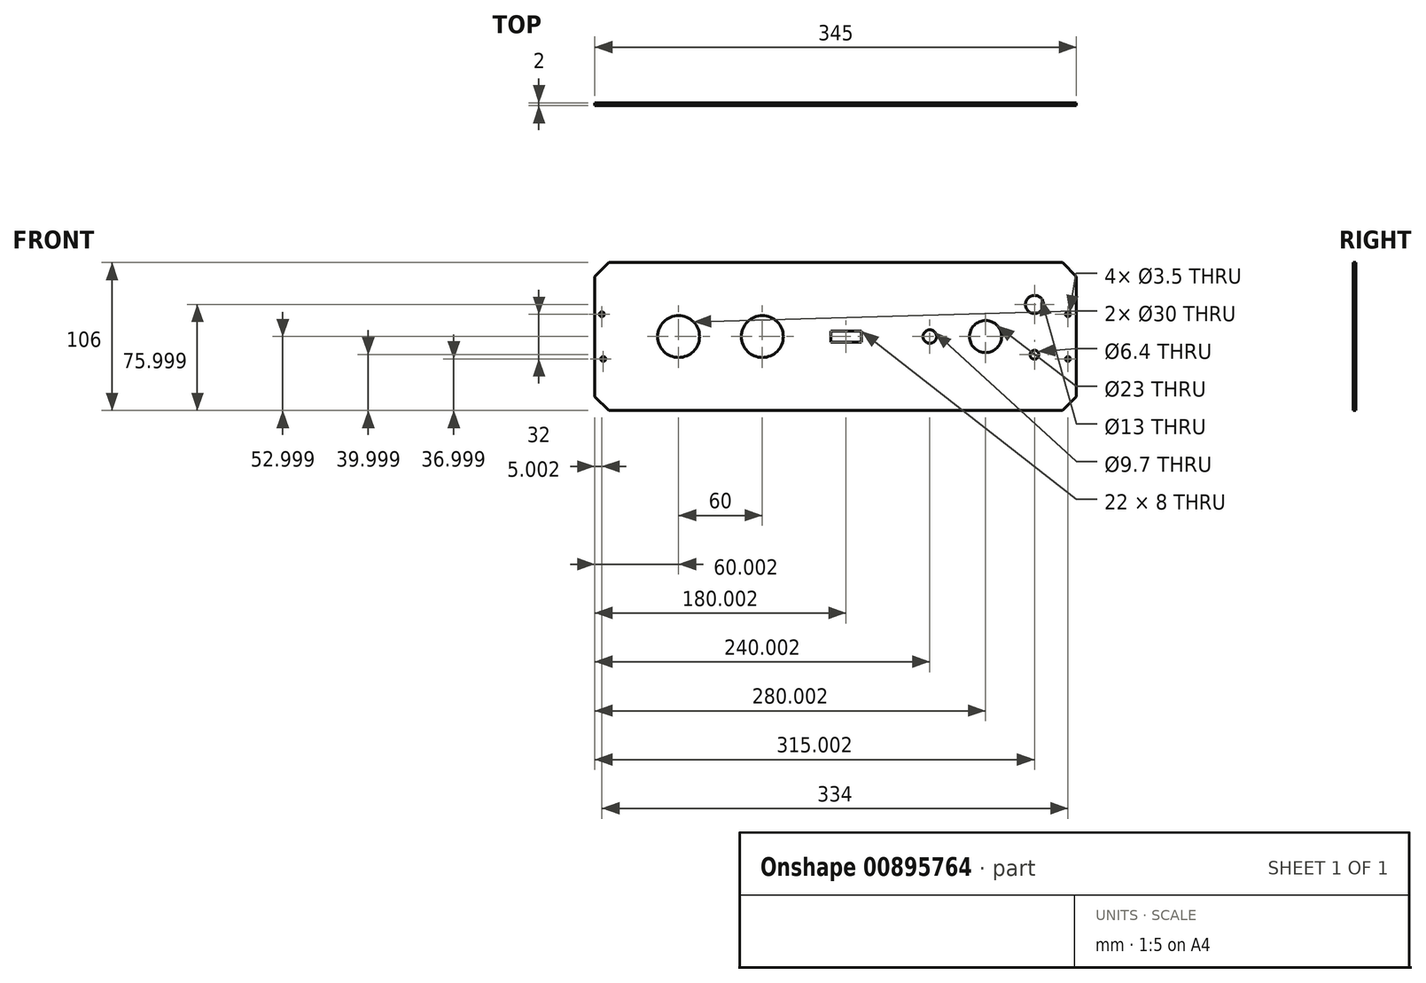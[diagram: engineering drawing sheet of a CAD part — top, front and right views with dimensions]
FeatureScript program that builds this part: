
annotation { "Feature Type Name" : "Feature", "Feature Type Description" : "" }
export const myFeature = defineFeature(function(context is Context, id is Id, definition is map)
    precondition{}
    {
        {
            var Q0;
            Q0=qCreatedBy(makeId("Front.planeOp"),FACE);
            var sketch = newSketch(context, id + "F0", { "sketchPlane" : qUnion([Q0])});
            skLineSegment(sketch, "E0.bottom", {"start": v(-126.34, 82.68) * mm, "end": v(218.66, 82.68) * mm});
            skLineSegment(sketch, "E0.top", {"start": v(-126.34, -23.32) * mm, "end": v(218.66, -23.32) * mm});
            skLineSegment(sketch, "E0.left", {"start": v(-126.34, 82.68) * mm, "end": v(-126.34, -23.32) * mm});
            skLineSegment(sketch, "E0.right", {"start": v(218.66, 82.68) * mm, "end": v(218.66, -23.32) * mm});
            skSolve(sketch);
        }
        {
            var Q0;
            Q0=makeQuery(id+"F0.imprint","IMPRINT",FACE,{"disambiguationData":[TD([[makeQuery(id+"F0.imprint","IMPRINT",EDGE,{"derivedFrom":sQuery(id+"F0.wireOp",EDGE,"E0.bottom")}),-1.0]])]});
            extrude(context, id + "F1", {"entities" : qUnion([Q0]), "depth" : 2 * mm, "offsetDistance" : 25 * mm});
        }
        {
            var Q0;
            Q0=makeQuery(id+"F1.opExtrude","SWEPT_EDGE",EDGE,{"disambiguationData":[OSD([sQuery(id+"F0.wireOp",EDGE,"E0.bottom"),sQuery(id+"F0.wireOp",EDGE,"E0.left")])]});
            chamfer(context, id + "F2", {"entities" : qUnion([Q0]), "width" : 10 * mm, "tangentPropagation" : true});
        }
        {
            var Q0;
            Q0=makeQuery(id+"F1.opExtrude","SWEPT_EDGE",EDGE,{"disambiguationData":[OSD([sQuery(id+"F0.wireOp",EDGE,"E0.top"),sQuery(id+"F0.wireOp",EDGE,"E0.left")])]});
            var Q1;
            Q1=makeQuery(id+"F1.opExtrude","SWEPT_EDGE",EDGE,{"disambiguationData":[OSD([sQuery(id+"F0.wireOp",EDGE,"E0.top"),sQuery(id+"F0.wireOp",EDGE,"E0.right")])]});
            var Q2;
            Q2=makeQuery(id+"F1.opExtrude","SWEPT_EDGE",EDGE,{"disambiguationData":[OSD([sQuery(id+"F0.wireOp",EDGE,"E0.bottom"),sQuery(id+"F0.wireOp",EDGE,"E0.right")])]});
            chamfer(context, id + "F3", {"entities" : qUnion([Q0, Q1, Q2]), "width" : 10 * mm, "tangentPropagation" : true});
        }
        {
            var Q0;
            Q0=makeQuery(id+"F1.opExtrude","CAP_FACE",FACE,{"disambiguationData":[OSD([sQuery(id+"F0.wireOp",EDGE,"E0.bottom"),sQuery(id+"F0.wireOp",EDGE,"E0.top"),sQuery(id+"F0.wireOp",EDGE,"E0.left"),sQuery(id+"F0.wireOp",EDGE,"E0.right")])],"isStart":false});
            var sketch = newSketch(context, id + "F4", { "sketchPlane" : qUnion([Q0])});
            skCircle(sketch, "E1", {"center": v(-121.34, 45.68) * mm, "radius": 1.75 * mm});
            skCircle(sketch, "E2", {"center": v(-120.34, 13.68) * mm, "radius": 1.75 * mm});
            skCircle(sketch, "E3", {"center": v(212.66, 45.68) * mm, "radius": 1.75 * mm});
            skCircle(sketch, "E4", {"center": v(212.66, 13.68) * mm, "radius": 1.75 * mm});
            skSolve(sketch);
        }
        {
            var Q0;
            Q0 = qSketchRegion(id + "F4", true);
            extrude(context, id + "F5", {"entities" : qUnion([Q0]), "operationType" : NewBodyOperationType.REMOVE, "oppositeDirection" : true, "depth" : 25 * mm, "offsetDistance" : 25 * mm});
        }
        {
            var Q0;
            Q0=makeQuery(id+"F1.opExtrude","CAP_FACE",FACE,{"disambiguationData":[OSD([sQuery(id+"F0.wireOp",EDGE,"E0.bottom"),sQuery(id+"F0.wireOp",EDGE,"E0.top"),sQuery(id+"F0.wireOp",EDGE,"E0.left"),sQuery(id+"F0.wireOp",EDGE,"E0.right")])],"isStart":false});
            var sketch = newSketch(context, id + "F6", { "sketchPlane" : qUnion([Q0])});
            skCircle(sketch, "E5", {"center": v(-66.34, 29.68) * mm, "radius": 15 * mm});
            skCircle(sketch, "E6", {"center": v(-6.34, 29.68) * mm, "radius": 15 * mm});
            skLineSegment(sketch, "E7.bottom", {"start": v(64.66, 33.68) * mm, "end": v(42.66, 33.68) * mm});
            skLineSegment(sketch, "E7.top", {"start": v(64.66, 25.68) * mm, "end": v(42.66, 25.68) * mm});
            skLineSegment(sketch, "E7.left", {"start": v(64.66, 33.68) * mm, "end": v(64.66, 25.68) * mm});
            skLineSegment(sketch, "E7.right", {"start": v(42.66, 33.68) * mm, "end": v(42.66, 25.68) * mm});
            skPoint(sketch, "E7.middle", {"position": v(53.66, 29.68) * mm});
            skPoint(sketch, "E8.middle", {"position": v(113.66, 29.68) * mm});
            skPoint(sketch, "E8.bottom.end.orphan", {"position": v(109.56, 38.1) * mm});
            skPoint(sketch, "E8.bottom.start.orphan", {"position": v(117.76, 38.1) * mm});
            skPoint(sketch, "E8.top.end.orphan", {"position": v(109.56, 21.27) * mm});
            skPoint(sketch, "E8.top.start.orphan", {"position": v(117.76, 21.27) * mm});
            skCircle(sketch, "E9", {"center": v(113.66, 29.68) * mm, "radius": 4.85 * mm});
            skSolve(sketch);
        }
        {
            var Q0;
            Q0=makeQuery(id+"F6.imprint","IMPRINT",FACE,{"disambiguationData":[TD([[makeQuery(id+"F6.imprint","IMPRINT",EDGE,{"derivedFrom":sQuery(id+"F6.wireOp",EDGE,"E5")}),1.0]])]});
            var Q1;
            Q1=makeQuery(id+"F6.imprint","IMPRINT",FACE,{"disambiguationData":[TD([[makeQuery(id+"F6.imprint","IMPRINT",EDGE,{"derivedFrom":sQuery(id+"F6.wireOp",EDGE,"E6")}),1.0]])]});
            var Q2;
            Q2=makeQuery(id+"F6.imprint","IMPRINT",FACE,{"disambiguationData":[TD([[makeQuery(id+"F6.imprint","IMPRINT",EDGE,{"derivedFrom":sQuery(id+"F6.wireOp",EDGE,"E7.bottom")}),1.0]])]});
            var Q3;
            Q3=makeQuery(id+"F6.imprint","IMPRINT",FACE,{"disambiguationData":[TD([[makeQuery(id+"F6.imprint","IMPRINT",EDGE,{"derivedFrom":sQuery(id+"F6.wireOp",EDGE,"ImCfHW0b-P2D1-mjxa-g2fg-wQ2FQqMqRvlU")}),1.0]])]});
            var Q4;
            Q4=makeQuery(id+"F6.imprint","IMPRINT",FACE,{"disambiguationData":[TD([[makeQuery(id+"F6.imprint","IMPRINT",EDGE,{"derivedFrom":sQuery(id+"F6.wireOp",EDGE,"oKTFB2zu-I9cH-oKnA-bQDt-sKLei0EZkSTM.bottom")}),1.0]])]});
            extrude(context, id + "F7", {"entities" : qUnion([Q0, Q1, Q2, Q3, Q4]), "operationType" : NewBodyOperationType.REMOVE, "oppositeDirection" : true, "depth" : 25 * mm, "offsetDistance" : 25 * mm});
        }
        {
            var Q0;
            Q0=makeQuery(id+"F1.opExtrude","CAP_FACE",FACE,{"disambiguationData":[OSD([sQuery(id+"F0.wireOp",EDGE,"E0.bottom"),sQuery(id+"F0.wireOp",EDGE,"E0.top"),sQuery(id+"F0.wireOp",EDGE,"E0.left"),sQuery(id+"F0.wireOp",EDGE,"E0.right")])],"isStart":false});
            var sketch = newSketch(context, id + "F8", { "sketchPlane" : qUnion([Q0])});
            skText(sketch, "E10", { "text": "1 = DC +\n2 = DC -\nMax = 40 V", "fontName": "NotoSans-Bold.ttf"});
            skText(sketch, "E11", { "text": "THERMOCOUPLE", "fontName": "OpenSans-Bold.ttf"});
            skPoint(sketch, "E11.firstSnap0", {"position": v(42.66, 29.68) * mm});
            skText(sketch, "E12", { "text": "BNC", "fontName": "OpenSans-Bold.ttf"});
            const initialGuessF8  = {"E10": [-0.07634, 0.06068, 1, 0, 0.002], "E10": [-0.07634, 0.06068, 1, 0, 0.002], "E10": [-0.07634, 0.06068, 1, 0, 0.002], "E10": [-0.07634, 0.06068, 1, 0, 0.002], "E11": [0.04266, 0.04368, 1, 0, 0.002], "E12": [0.11015, 0.04172, 1, 0, 0.002]};
            skSetInitialGuess(sketch, initialGuessF8);
            skSolve(sketch);
        }
        {
            var Q0;
            Q0=makeQuery(id+"F8.imprint","IMPRINT",FACE,{"disambiguationData":[TD([[makeQuery(id+"F8.imprint","IMPRINT",EDGE,{"derivedFrom":sQuery(id+"F8.wireOp",EDGE,"E10.sketch_text.stroke-0")}),1.0]])]});
            var sketch = newSketch(context, id + "F9", { "sketchPlane" : qUnion([Q0])});
            skCircle(sketch, "E13", {"center": v(188.66, 52.68) * mm, "radius": 6.5 * mm});
            skCircle(sketch, "E14", {"center": v(153.66, 29.68) * mm, "radius": 11.5 * mm});
            skCircle(sketch, "E15", {"center": v(188.66, 16.68) * mm, "radius": 3.2 * mm});
            skSolve(sketch);
        }
        {
            var Q0;
            Q0 = qSketchRegion(id + "F9", true);
            extrude(context, id + "F10", {"entities" : qUnion([Q0]), "operationType" : NewBodyOperationType.REMOVE, "oppositeDirection" : true, "depth" : 25 * mm, "offsetDistance" : 25 * mm});
        }
        {
            var Q0;
            Q0 = qSketchRegion(id + "F6", true);
            extrude(context, id + "F11", {"entities" : qUnion([Q0]), "operationType" : NewBodyOperationType.REMOVE, "oppositeDirection" : true, "depth" : 25 * mm, "offsetDistance" : 25 * mm});
        }
    });
